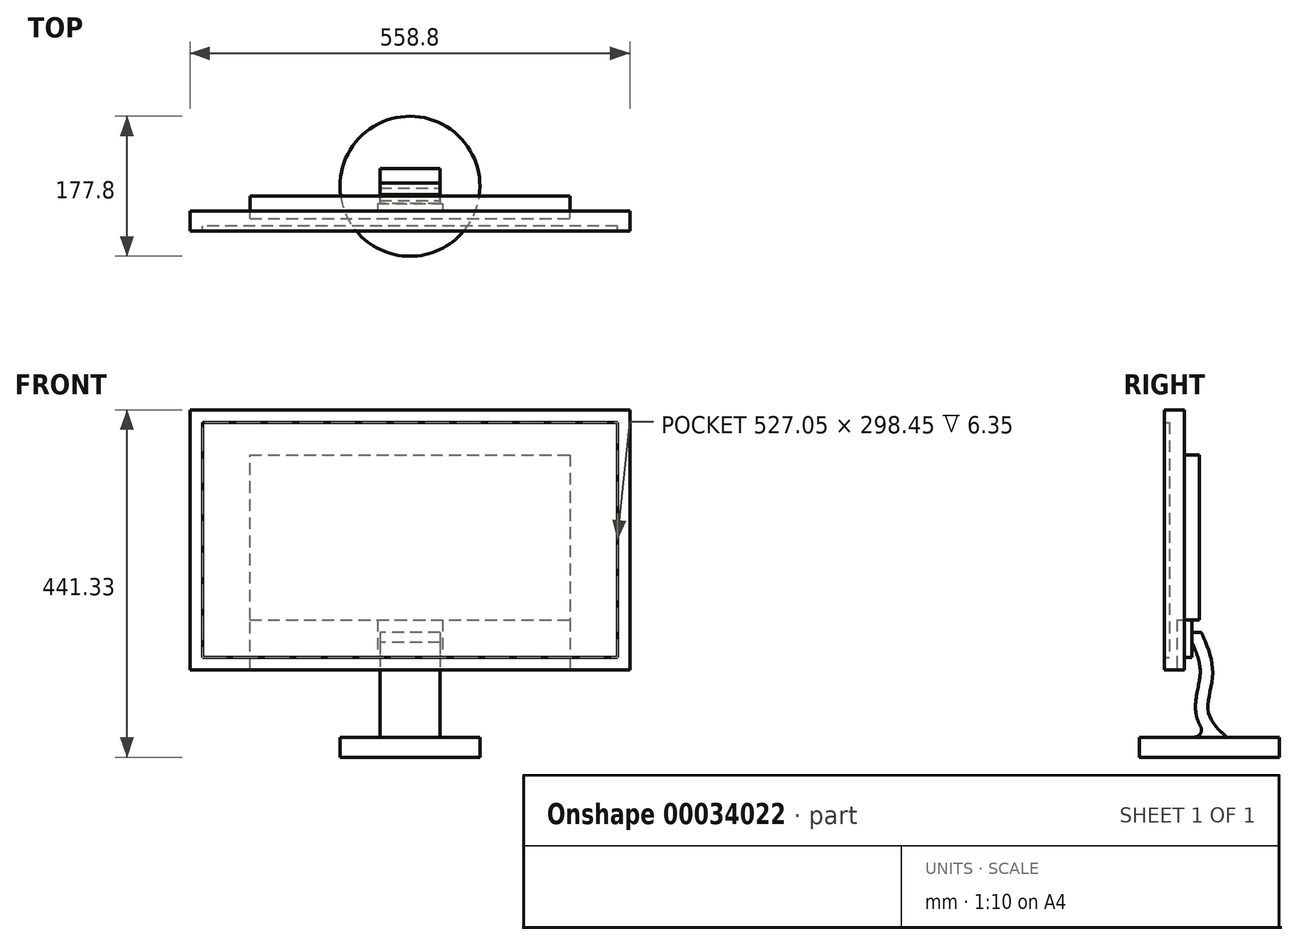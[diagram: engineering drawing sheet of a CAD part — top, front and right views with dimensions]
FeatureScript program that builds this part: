
annotation { "Feature Type Name" : "Feature", "Feature Type Description" : "" }
export const myFeature = defineFeature(function(context is Context, id is Id, definition is map)
    precondition{}
    {
        {
            var Q0;
            Q0=qCreatedBy(makeId("Front.planeOp"),FACE);
            var sketch = newSketch(context, id + "F0", { "sketchPlane" : qUnion([Q0])});
            skLineSegment(sketch, "E0.bottom", {"start": v(-289.1, 187.95) * mm, "end": v(269.7, 187.95) * mm});
            skLineSegment(sketch, "E0.top", {"start": v(-289.1, -142.25) * mm, "end": v(269.7, -142.25) * mm});
            skLineSegment(sketch, "E0.left", {"start": v(-289.1, 187.95) * mm, "end": v(-289.1, -142.25) * mm});
            skLineSegment(sketch, "E0.right", {"start": v(269.7, 187.95) * mm, "end": v(269.7, -142.25) * mm});
            skLineSegment(sketch, "E1", {"start": v(-273.23, 172.07) * mm, "end": v(-273.23, -126.38) * mm});
            skLineSegment(sketch, "E2", {"start": v(-273.23, -126.38) * mm, "end": v(253.82, -126.38) * mm});
            skLineSegment(sketch, "E3", {"start": v(253.82, -126.38) * mm, "end": v(253.82, 172.07) * mm});
            skLineSegment(sketch, "E4", {"start": v(253.82, 172.07) * mm, "end": v(-273.23, 172.07) * mm});
            skSolve(sketch);
        }
        {
            var Q0;
            Q0=makeQuery(id+"F0.imprint","IMPRINT",FACE,{"disambiguationData":[TD([[makeQuery(id+"F0.imprint","IMPRINT",EDGE,{"derivedFrom":sQuery(id+"F0.wireOp",EDGE,"E0.bottom")}),-1.0]])]});
            extrude(context, id + "F1", {"entities" : qUnion([Q0]), "depth" : 25.4 * mm});
        }
        {
            var Q0;
            Q0=makeQuery(id+"F0.imprint","IMPRINT",FACE,{"disambiguationData":[TD([[makeQuery(id+"F0.imprint","IMPRINT",EDGE,{"derivedFrom":sQuery(id+"F0.wireOp",EDGE,"E1")}),1.0]])]});
            extrude(context, id + "F2", {"entities" : qUnion([Q0]), "operationType" : NewBodyOperationType.ADD, "depth" : 19.05 * mm});
        }
        {
            var Q0;
            Q0=makeQuery(id+"F0.imprint","IMPRINT",FACE,{"disambiguationData":[TD([[makeQuery(id+"F0.imprint","IMPRINT",EDGE,{"derivedFrom":sQuery(id+"F0.wireOp",EDGE,"E1")}),1.0]])]});
            var sketch = newSketch(context, id + "F3", { "sketchPlane" : qUnion([Q0])});
            skLineSegment(sketch, "E5", {"start": v(-212.9, 130.8) * mm, "end": v(193.5, 130.8) * mm});
            skLineSegment(sketch, "E6", {"start": v(193.5, 130.8) * mm, "end": v(193.5, -78.75) * mm});
            skLineSegment(sketch, "E7", {"start": v(193.5, -78.75) * mm, "end": v(-212.9, -78.75) * mm});
            skLineSegment(sketch, "E8", {"start": v(-212.9, -78.75) * mm, "end": v(-212.9, 130.8) * mm});
            skSolve(sketch);
        }
        {
            var Q0;
            Q0=makeQuery(id+"F3.imprint","IMPRINT",FACE,{"disambiguationData":[TD([[makeQuery(id+"F3.imprint","IMPRINT",EDGE,{"derivedFrom":sQuery(id+"F3.wireOp",EDGE,"E5")}),-1.0]])]});
            extrude(context, id + "F4", {"entities" : qUnion([Q0]), "operationType" : NewBodyOperationType.ADD, "oppositeDirection" : true, "depth" : 19.05 * mm});
        }
        {
            var Q0;
            Q0=makeQuery(id+"F0.imprint","IMPRINT",FACE,{"disambiguationData":[TD([[makeQuery(id+"F0.imprint","IMPRINT",EDGE,{"derivedFrom":sQuery(id+"F0.wireOp",EDGE,"E1")}),1.0]])]});
            var sketch = newSketch(context, id + "F5", { "sketchPlane" : qUnion([Q0])});
            skPoint(sketch, "E9.0", {"position": v(193.5, -78.75) * mm});
            skPoint(sketch, "E10.0", {"position": v(-212.9, -78.75) * mm});
            skLineSegment(sketch, "E11", {"start": v(193.5, -78.75) * mm, "end": v(193.5, -142.25) * mm});
            skLineSegment(sketch, "E12", {"start": v(193.5, -142.25) * mm, "end": v(-212.9, -142.25) * mm});
            skLineSegment(sketch, "E13", {"start": v(-212.9, -142.25) * mm, "end": v(-212.9, -78.75) * mm});
            skLineSegment(sketch, "E14", {"start": v(-212.9, -78.75) * mm, "end": v(193.5, -78.75) * mm});
            skSolve(sketch);
        }
        {
            var Q0;
            {var subQ5=sQuery(id+"F5.wireOp",EDGE,"E12");Q0=makeQuery(id+"F5.imprint","IMPRINT",FACE,{"disambiguationData":[TD([[makeQuery(id+"F5.imprint","IMPRINT",EDGE,{"derivedFrom":subQ5}),-1.0]])]});}
            var Q1;
            {var subQ5=sQuery(id+"F5.wireOp",EDGE,"E14");Q1=makeQuery(id+"F5.imprint","IMPRINT",FACE,{"disambiguationData":[TD([[makeQuery(id+"F5.imprint","IMPRINT",EDGE,{"derivedFrom":subQ5}),-1.0]])]});}
            extrude(context, id + "F6", {"entities" : qUnion([Q0, Q1]), "operationType" : NewBodyOperationType.REMOVE, "depth" : 9.52 * mm});
        }
        {
            var Q0;
            {var subQ5=sQuery(id+"F5.wireOp",EDGE,"E14");Q0=makeQuery(id+"F5.imprint","IMPRINT",FACE,{"disambiguationData":[TD([[makeQuery(id+"F5.imprint","IMPRINT",EDGE,{"derivedFrom":subQ5}),-1.0]])]});}
            var sketch = newSketch(context, id + "F7", { "sketchPlane" : qUnion([Q0])});
            skLineSegment(sketch, "E15", {"start": v(31.57, -126.38) * mm, "end": v(-50.98, -126.38) * mm});
            skPoint(sketch, "E16.0", {"position": v(-212.9, -78.75) * mm});
            skLineSegment(sketch, "E17", {"start": v(-50.98, -78.75) * mm, "end": v(31.57, -78.75) * mm});
            skLineSegment(sketch, "E18", {"start": v(-50.98, -78.75) * mm, "end": v(-50.98, -126.38) * mm});
            skLineSegment(sketch, "E19", {"start": v(32, -78.67) * mm, "end": v(31.57, -126.38) * mm});
            skSolve(sketch);
        }
        {
            var Q0;
            {var subQ5=sQuery(id+"F7.wireOp",EDGE,"E15");Q0=makeQuery(id+"F7.imprint","IMPRINT",FACE,{"disambiguationData":[TD([[makeQuery(id+"F7.imprint","IMPRINT",EDGE,{"derivedFrom":subQ5}),1.0]])]});}
            extrude(context, id + "F8", {"entities" : qUnion([Q0]), "operationType" : NewBodyOperationType.ADD, "oppositeDirection" : true, "depth" : 9.52 * mm});
        }
        {
            var Q0;
            Q0=makeQuery(id+"F8.opExtrude","CAP_FACE",FACE,{"disambiguationData":[OSD([sQuery(id+"F5.wireOp",EDGE,"E14"),sQuery(id+"F7.wireOp",EDGE,"E15"),sQuery(id+"F7.wireOp",EDGE,"E17"),sQuery(id+"F7.wireOp",EDGE,"E18"),sQuery(id+"F7.wireOp",EDGE,"E19")])],"isStart":false});
            var sketch = newSketch(context, id + "F9", { "sketchPlane" : qUnion([Q0])});
            skLineSegment(sketch, "E20", {"start": v(-28.68, -94.63) * mm, "end": v(47.8, -94.63) * mm});
            skLineSegment(sketch, "E21", {"start": v(47.8, -94.63) * mm, "end": v(47.8, -126.38) * mm});
            skLineSegment(sketch, "E22", {"start": v(47.8, -126.38) * mm, "end": v(-28.68, -126.38) * mm});
            skLineSegment(sketch, "E23", {"start": v(-28.68, -94.63) * mm, "end": v(-28.68, -126.38) * mm});
            skSolve(sketch);
        }
        {
            var Q0;
            Q0=makeQuery(id+"F9.imprint","IMPRINT",FACE,{"disambiguationData":[TD([[makeQuery(id+"F9.imprint","IMPRINT",EDGE,{"derivedFrom":sQuery(id+"F9.wireOp",EDGE,"E20")}),-1.0]])]});
            extrude(context, id + "F10", {"entities" : qUnion([Q0]), "operationType" : NewBodyOperationType.ADD, "depth" : 44.45 * mm});
        }
        {
            var Q0;
            Q0=makeQuery(id+"F10.boolean.opBoolean","MERGE",FACE,{"derivedFrom":[makeQuery(id+"F8.opExtrude","SWEPT_FACE",FACE,{"disambiguationData":[OSD([sQuery(id+"F7.wireOp",EDGE,"E15")])]}),makeQuery(id+"F10.opExtrude","SWEPT_FACE",FACE,{"disambiguationData":[OSD([sQuery(id+"F9.wireOp",EDGE,"E22")])]})]});
            var sketch = newSketch(context, id + "F11", { "sketchPlane" : qUnion([Q0])});
            skLineSegment(sketch, "E24", {"start": v(28.68, -9.53) * mm, "end": v(-47.8, -9.53) * mm});
            skLineSegment(sketch, "E25", {"start": v(-47.8, -9.52) * mm, "end": v(-47.8, -53.98) * mm});
            skLineSegment(sketch, "E26", {"start": v(-47.8, -53.98) * mm, "end": v(28.68, -53.98) * mm});
            skLineSegment(sketch, "E27", {"start": v(28.68, -53.98) * mm, "end": v(28.68, -9.52) * mm});
            skSolve(sketch);
        }
        {
            var Q0;
            Q0=makeQuery(id+"F11.imprint","IMPRINT",FACE,{"disambiguationData":[TD([[makeQuery(id+"F11.imprint","IMPRINT",EDGE,{"derivedFrom":sQuery(id+"F11.wireOp",EDGE,"E24")}),1.0]])]});
            extrude(context, id + "F12", {"entities" : qUnion([Q0]), "operationType" : NewBodyOperationType.ADD, "depth" : 101.6 * mm});
        }
        {
            var Q0;
            Q0=makeQuery(id+"F12.opExtrude","CAP_FACE",FACE,{"disambiguationData":[OSD([sQuery(id+"F11.wireOp",EDGE,"E24"),sQuery(id+"F11.wireOp",EDGE,"E25"),sQuery(id+"F11.wireOp",EDGE,"E26"),sQuery(id+"F11.wireOp",EDGE,"E27")])],"isStart":false});
            var sketch = newSketch(context, id + "F13", { "sketchPlane" : qUnion([Q0])});
            skCircle(sketch, "E28", {"center": v(-9.56, -31.75) * mm, "radius": 88.9 * mm});
            skPoint(sketch, "E28.centerSnap0", {"position": v(-9.56, -53.98) * mm});
            skPoint(sketch, "E28.centerSnap1", {"position": v(28.68, -31.75) * mm});
            skSolve(sketch);
        }
        {
            var Q0;
            Q0 = qSketchRegion(id + "F13", true);
            extrude(context, id + "F14", {"entities" : qUnion([Q0]), "operationType" : NewBodyOperationType.ADD, "depth" : 25.4 * mm});
        }
        {
            var Q0;
            Q0=makeQuery(id+"F12.boolean.opBoolean","MERGE",FACE,{"derivedFrom":[makeQuery(id+"F10.opExtrude","SWEPT_FACE",FACE,{"disambiguationData":[OSD([sQuery(id+"F9.wireOp",EDGE,"E21")])]}),makeQuery(id+"F12.opExtrude","SWEPT_FACE",FACE,{"disambiguationData":[OSD([sQuery(id+"F11.wireOp",EDGE,"E25")])]})]});
            var sketch = newSketch(context, id + "F15", { "sketchPlane" : qUnion([Q0])});
            skFitSpline(sketch, "E29", {"points": [v(-21.2, -94.63) * mm, v(-35.71, -146.34) * mm, v(-30.35, -196.38) * mm, v(-53.98, -227.98) * mm], "startDerivative": vector(-63.14, -143.08) * mm, "endDerivative": vector(-104.86, -93.64) * mm});
            skFitSpline(sketch, "E30.0", {"points": [v(-6.68, -101.04) * mm, v(-8, -104.02) * mm, v(-10.57, -109.85) * mm, v(-14.01, -118.26) * mm, v(-16.36, -124.97) * mm, v(-17.83, -130.15) * mm, v(-18.7, -133.95) * mm, v(-19.35, -137.66) * mm, v(-19.68, -140.68) * mm, v(-19.82, -143.06) * mm, v(-19.86, -144.54) * mm, v(-19.85, -145.72) * mm, v(-19.82, -146.9) * mm, v(-19.74, -148.44) * mm, v(-19.58, -150.36) * mm, v(-19.27, -153.02) * mm, v(-18.75, -156.52) * mm, v(-17.95, -160.96) * mm, v(-17.04, -165.6) * mm, v(-16.1, -170.43) * mm, v(-15.19, -175.44) * mm, v(-14.43, -180.62) * mm, v(-13.93, -186.02) * mm, v(-13.84, -190.72) * mm, v(-14.07, -194.6) * mm, v(-14.36, -197.09) * mm, v(-14.66, -198.85) * mm, v(-14.85, -199.86) * mm, v(-15.17, -201.36) * mm, v(-15.74, -203.57) * mm, v(-16.67, -206.4) * mm, v(-17.75, -209.12) * mm, v(-18.97, -211.7) * mm, v(-20.74, -215) * mm, v(-23.2, -218.84) * mm, v(-26.4, -223.02) * mm, v(-29.75, -226.85) * mm, v(-33.18, -230.4) * mm, v(-37.8, -234.82) * mm, v(-41.22, -237.87) * mm, v(-43.4, -239.82) * mm]});
            skLineSegment(sketch, "E31.0", {"start": v(-15.88, -126.38) * mm, "end": v(-15.88, -100.98) * mm});
            skLineSegment(sketch, "E31.1", {"start": v(-15.88, -221.63) * mm, "end": v(-15.88, -126.38) * mm});
            skLineSegment(sketch, "E31.2", {"start": v(-47.62, -221.63) * mm, "end": v(-15.87, -221.63) * mm});
            skLineSegment(sketch, "E31.3", {"start": v(-47.62, -100.98) * mm, "end": v(-47.62, -221.63) * mm});
            skLineSegment(sketch, "E31.4", {"start": v(-15.88, -100.98) * mm, "end": v(-47.62, -100.98) * mm});
            skSolve(sketch);
        }
        {
            var Q0;
            {var subQ3=sQuery(id+"F15.wireOp",EDGE,"E31.3");Q0=makeQuery(id+"F15.imprint","IMPRINT",FACE,{"disambiguationData":[TD([[makeQuery(id+"F15.imprint","IMPRINT",EDGE,{"derivedFrom":subQ3}),1.0]])]});}
            var Q1;
            {var subQ8=sQuery(id+"F15.wireOp",EDGE,"E31.3");Q1=makeQuery(id+"F15.imprint","IMPRINT",FACE,{"disambiguationData":[TD([[makeQuery(id+"F15.imprint","IMPRINT",EDGE,{"derivedFrom":subQ8}),-1.0]])]});}
            var Q2;
            {var subQ1=sQuery(id+"F15.wireOp",EDGE,"E30.0");var subQ3=sQuery(id+"F15.wireOp",EDGE,"E31.0");var subQ5=makeQuery(id+"F15.imprint","INTERSECT",VERTEX,{"derivedFrom":[subQ1,subQ3]});Q2=makeQuery(id+"F15.imprint","IMPRINT",FACE,{"disambiguationData":[TD([[makeQuery(id+"F15.imprint","IMPRINT",EDGE,{"disambiguationData":[TD([[subQ5,-1.0]])],"derivedFrom":subQ1}),1.0]])]});}
            var Q3;
            {var subQ0=sQuery(id+"F11.wireOp",EDGE,"E25");var subQ4=makeQuery(id+"F12.opExtrude","SWEPT_EDGE",EDGE,{"disambiguationData":[OSD([sQuery(id+"F7.wireOp",EDGE,"E15"),sQuery(id+"F11.wireOp",EDGE,"E24"),subQ0])]});Q3=makeQuery(id+"F15.imprint","IMPRINT",FACE,{"disambiguationData":[TD([[makeQuery(id+"F15.imprint","IMPRINT",EDGE,{"derivedFrom":subQ4}),1.0]])]});}
            var Q4;
            {var subQ1=sQuery(id+"F15.wireOp",EDGE,"E30.0");var subQ3=sQuery(id+"F15.wireOp",EDGE,"E31.1");var subQ5=makeQuery(id+"F15.imprint","INTERSECT",VERTEX,{"disambiguationData":[OD(1.0)],"derivedFrom":[subQ1,subQ3]});Q4=makeQuery(id+"F15.imprint","IMPRINT",FACE,{"disambiguationData":[TD([[makeQuery(id+"F15.imprint","IMPRINT",EDGE,{"disambiguationData":[TD([[subQ5,-1.0]])],"derivedFrom":subQ1}),1.0]])]});}
            extrude(context, id + "F16", {"entities" : qUnion([Q0, Q1, Q2, Q3, Q4]), "operationType" : NewBodyOperationType.REMOVE, "endBound" : BoundingType.UP_TO_NEXT, "oppositeDirection" : true, "depth" : 25.4 * mm});
        }
        {
            var Q0;
            Q0=makeQuery(id+"F16.boolean.opBoolean","COPY",EDGE,{"derivedFrom":makeQuery(id+"F16.opExtrude","SWEPT_EDGE",EDGE,{"disambiguationData":[OSD([sQuery(id+"F9.wireOp",EDGE,"E20"),sQuery(id+"F9.wireOp",EDGE,"E21"),sQuery(id+"F15.wireOp",EDGE,"E29")])]})});
            var Q1;
            {var subQ0=sQuery(id+"F11.wireOp",EDGE,"E26");Q1=makeQuery(id+"F16.boolean.opBoolean","MERGE",EDGE,{"derivedFrom":[makeQuery(id+"F12.opExtrude","CAP_EDGE",EDGE,{"disambiguationData":[OSD([subQ0])],"isStart":false}),makeQuery(id+"F16.opExtrude","SWEPT_EDGE",EDGE,{"disambiguationData":[OSD([subQ0,sQuery(id+"F11.wireOp",EDGE,"E27")])]})]});}
            var Q2;
            Q2=makeQuery(id+"F16.boolean.opBoolean","COPY",EDGE,{"derivedFrom":makeQuery(id+"F16.opExtrude","SWEPT_EDGE",EDGE,{"disambiguationData":[OSD([sQuery(id+"F11.wireOp",EDGE,"E25"),sQuery(id+"F15.wireOp",EDGE,"E30.0")])]})});
            var Q3;
            Q3=makeQuery(id+"F12.opExtrude","CAP_EDGE",EDGE,{"disambiguationData":[OSD([sQuery(id+"F11.wireOp",EDGE,"E25")])],"isStart":false});
            var Q4;
            Q4=makeQuery(id+"F12.opExtrude","CAP_EDGE",EDGE,{"disambiguationData":[OSD([sQuery(id+"F11.wireOp",EDGE,"E27")])],"isStart":false});
            fillet(context, id + "F17", {"entities" : qUnion([Q0, Q1, Q2, Q3, Q4]), "radius" : 9.34 * mm, "tangentPropagation" : true, "allowEdgeOverflow" : false});
        }
    });
